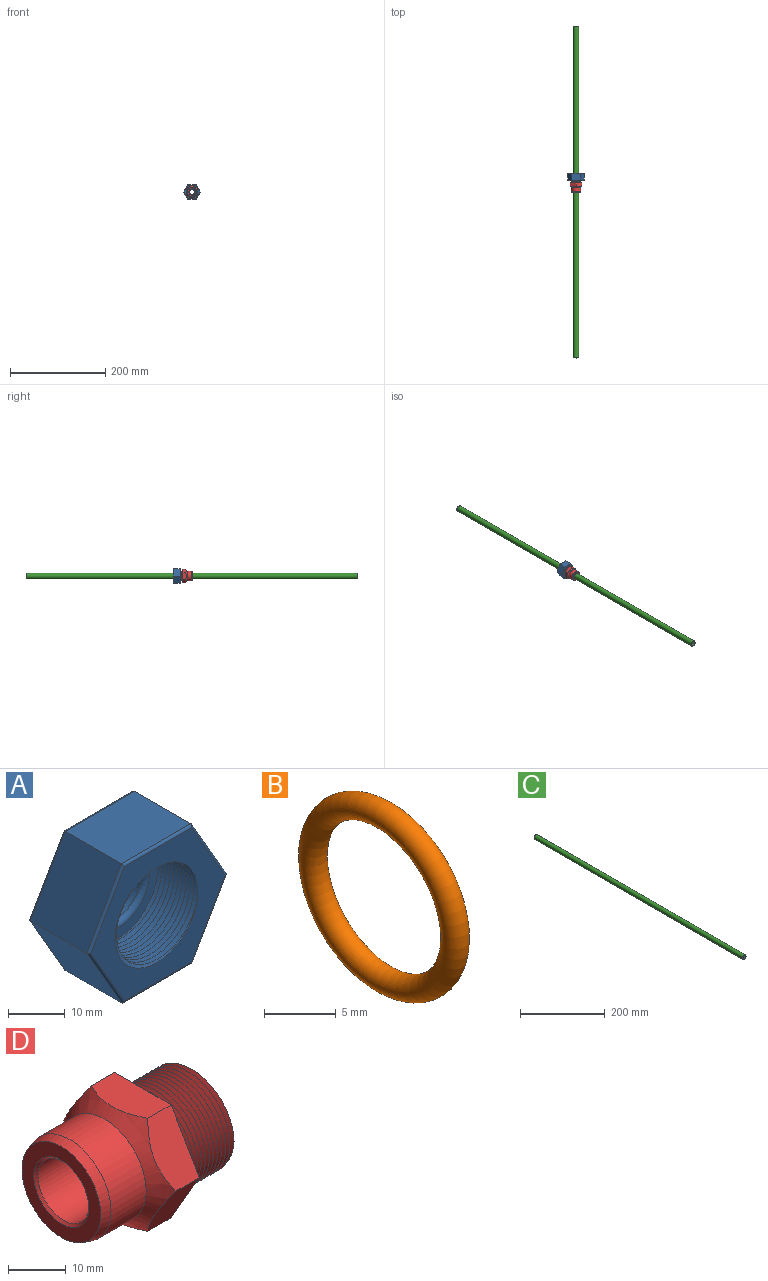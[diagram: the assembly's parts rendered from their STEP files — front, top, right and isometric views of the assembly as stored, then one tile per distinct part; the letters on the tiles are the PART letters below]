
ASSEMBLY  parts=4 mates=3
PART A: 27 faces, bbox 35.4x16.4x30.8 mm
  f0: bspline ~24.71x21.4mm, area 643.3mm2, adj f1,f9,f10,f12
  f1: bspline ~24.71x21.4mm, area 643.3mm2, adj f0,f9,f10,f12
  f2: plane 15x14mm, normal (0.87,0,0.5), area 242.5mm2, adj f3,f7,f17,f23
  f3: plane 17.32x14mm, normal (0,0,1), area 242.5mm2, adj f2,f4,f15,f21
  f4: plane 15x14mm, normal (-0.87,0,0.5), area 242.5mm2, adj f3,f5,f16,f22
  f5: plane 15x14mm, normal (-0.87,0,-0.5), area 242.5mm2, adj f4,f6,f18,f24
  f6: plane 17.32x14mm, normal (0,0,-1), area 242.5mm2, adj f5,f7,f20,f26
  f7: plane 15x14mm, normal (0.87,0,-0.5), area 242.5mm2, adj f2,f6,f19,f25
  f8: plane 33.49x29mm, normal (0,1,0), area 556.3mm2, adj f14,f21,f22,f23,f24,f25,f26
  f9: plane 34.26x29.77mm, normal (0,-1,0), area 396.9mm2, adj f0,f1,f10,f15,f16,f17,f18,f19
  f10: cylinder r=10.7mm len=21.4mm, axis (0,-1,0), area -0.5mm2, adj f0,f1,f9,f12
  f11: cylinder r=6.9mm len=13.8mm, axis (0,1,0), area 151.7mm2, adj f13,f14
  f12: plane 21.33x21.32mm, normal (0,-1,0), area 135.3mm2, adj f0,f1,f10,f13
  f13: torus R=7.9mm, axis (0,-1,0), area 71.7mm2, adj f11,f12
  f14: torus R=7.4mm, axis (0,-1,0), area 34.9mm2, adj f8,f11
  f15: cylinder r=0.5mm len=17.32mm, axis (-1,0,0), area 13.4mm2, adj f3,f9,f16,f17
  f16: cylinder r=0.5mm len=15.25mm, axis (-0.5,0,-0.87), area 13.4mm2, adj f4,f9,f15,f18
  f17: cylinder r=0.5mm len=15.25mm, axis (-0.5,0,0.87), area 13.4mm2, adj f2,f9,f15,f19
  f18: cylinder r=0.5mm len=15.25mm, axis (0.5,0,-0.87), area 13.4mm2, adj f5,f9,f16,f20
  f19: cylinder r=0.5mm len=15.25mm, axis (0.5,0,0.87), area 13.4mm2, adj f7,f9,f17,f20
  f20: cylinder r=0.5mm len=17.32mm, axis (1,0,0), area 13.4mm2, adj f6,f9,f18,f19
  f21: cylinder r=0.5mm len=17.32mm, axis (1,0,0), area 13.4mm2, adj f3,f8,f22,f23
  f22: cylinder r=0.5mm len=15.25mm, axis (0.5,0,0.87), area 13.4mm2, adj f4,f8,f21,f24
  f23: cylinder r=0.5mm len=15.25mm, axis (0.5,0,-0.87), area 13.4mm2, adj f2,f8,f21,f25
  f24: cylinder r=0.5mm len=15.25mm, axis (-0.5,0,0.87), area 13.4mm2, adj f5,f8,f22,f26
  f25: cylinder r=0.5mm len=15.25mm, axis (-0.5,0,-0.87), area 13.4mm2, adj f7,f8,f23,f26
  f26: cylinder r=0.5mm len=17.32mm, axis (-1,0,0), area 13.4mm2, adj f6,f8,f24,f25
PART B: 1 faces, bbox 2x17.3x17.3 mm
  f0: torus R=7mm, axis (-1,0,0), area 276.3mm2
PART C: 4 faces, bbox 12x696x12 mm
  f0: cylinder r=5mm len=696mm, axis (0,-1,0), area 21865.5mm2, adj f2,f3
  f1: cylinder r=6mm len=694mm, axis (0,-1,0), area 26163.2mm2, adj f2,f3
  f2: cone r=6mm half-angle=45deg, axis (0,-1,0), area 48.9mm2, adj f0,f1
  f3: cone r=5mm half-angle=45deg, axis (0,1,0), area 48.9mm2, adj f0,f1
PART D: 18 faces, bbox 34.4x29.4x29.4 mm
  f0: bspline ~23.94x20.73mm, area 383.6mm2, adj f1,f2,f3,f5
  f1: bspline ~23.94x20.73mm, area 750.7mm2, adj f0,f2,f3,f5
  f2: cylinder r=9.5mm len=19mm, axis (-1,0,0), area 0mm2, adj f0,f1
  f3: plane 20.64x20.64mm, normal (1,0,0), area 101.4mm2, adj f0,f1,f10
  f4: cylinder r=6.25mm len=30.4mm, axis (-1,0,0), area 1193.9mm2, adj f8,f10
  f5: plane 29.44x25.73mm, normal (1,0,0), area 188.7mm2, adj f0,f1,f11,f12,f13,f14,f15,f16
  f6: cylinder r=10.2mm len=20.4mm, axis (1,0,0), area 551.2mm2, adj f9,f17
  f7: plane 19.33x19.33mm, normal (-1,0,0), area 150.3mm2, adj f8,f9
  f8: cone r=6.75mm half-angle=45deg, axis (-1,0,0), area 28.9mm2, adj f4,f7
  f9: cone r=10.2mm half-angle=15deg, axis (1,0,0), area 129.2mm2, adj f6,f7
  f10: cone r=8.15mm half-angle=60deg, axis (1,0,0), area 99.3mm2, adj f3,f4
  f11: plane 15.21x8.96mm, normal (0,0,-1), area 96.5mm2, adj f5,f12,f16,f17
  f12: plane 12x7.6mm, normal (0,-0.87,-0.5), area 96.5mm2, adj f5,f11,f13,f17
  f13: plane 12x7.6mm, normal (0,-0.87,0.5), area 96.5mm2, adj f5,f12,f14,f17
  f14: plane 13.86x7.6mm, normal (0,0,1), area 96.5mm2, adj f5,f13,f15,f17
  f15: plane 12x7.6mm, normal (0,0.87,0.5), area 96.5mm2, adj f5,f14,f16,f17
  f16: plane 12x7.6mm, normal (0,0.87,-0.5), area 96.5mm2, adj f5,f11,f15,f17
  f17: cone r=14.6mm half-angle=45deg, axis (1,0,0), area 247.6mm2, adj f6,f11,f12,f13,f14,f15,f16
PLACE A t=(0,372.26,0)mm
PLACE B rot(axis=(-0.58,-0.58,0.58),120deg) t=(0,379.8,0)mm
PLACE C at identity
PLACE D rot(axis=(-0.58,-0.58,0.58),120deg) t=(0,367.5,0)mm
MATE slider B.f0 <-> C.f1  axis (0,-1,0) through (0,379.8,0)mm
MATE fastened D.f2 <-> C.f1  axis (0,-1,0) through (0,348,0)mm
MATE slider C.f1 <-> A.f10  axis (0,-1,0) through (0,348,0)mm
